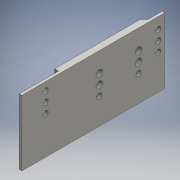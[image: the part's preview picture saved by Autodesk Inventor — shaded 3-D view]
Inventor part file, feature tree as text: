
AUTODESK INVENTOR PART (.ipt)
format: ipt  version: 2016 (Build 200138000, 138)  size: 148,480 bytes
history: native  units: mm
features: extrude x3, sketch x3
ambient origin geometry x8: Origin, YZ Plane, XZ Plane, XY Plane, X Axis, Y Axis, Z Axis, Center Point
bodies: Solid1 (feature_tree)
feature tree (6):
  extrude  "Extrusion1"  Depth=218.0mm
  extrude  "Extrusion2"  Depth=4.0mm
  extrude  "Extrusion3"  TaperAngle=135.0deg  [1 undecoded]
  sketch  "Sketch1"  dims[d0=100.0mm d1=218.0mm]
  sketch  "Sketch2"  dims[d2=10.0mm d3=0.0mm d5=4.0mm]
  sketch  "Sketch3"  dims[d6=22.0mm d7=135.0deg d8=60.0mm d10=4.0mm d11=10.0mm d12=0.0mm d13=8.0mm d14=8.0mm d15=17.0mm d16=15.0mm d17=15.0mm d18=10.0mm d19=12.0mm d20=15.0mm d21=15.0mm d22=36.0mm d23=10.0mm d24=8.0mm d25=40.0mm d26=30.0mm d27=15.0mm d28=15.0mm d29=60.0mm d30=15.0mm d31=15.0mm d32=10.0mm d33=0.0mm]
note: 1 required parameter value undecoded (feature->parameter linkage not recoverable at this tier; creation-order binding heuristic only, values carry confidence <= 0.55)
